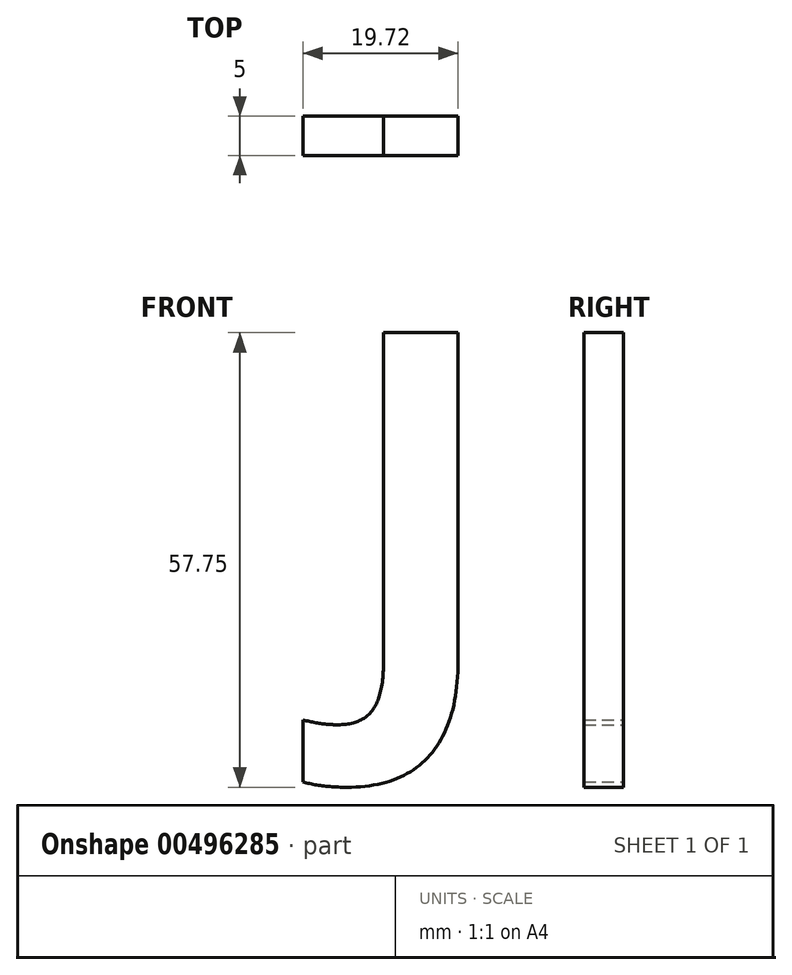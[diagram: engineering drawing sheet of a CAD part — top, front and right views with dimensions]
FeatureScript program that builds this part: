
annotation { "Feature Type Name" : "Feature", "Feature Type Description" : "" }
export const myFeature = defineFeature(function(context is Context, id is Id, definition is map)
    precondition{}
    {
        {
            var Q0;
            Q0=qCreatedBy(makeId("Front.planeOp"),FACE);
            var sketch = newSketch(context, id + "F0", { "sketchPlane" : qUnion([Q0])});
            skText(sketch, "E0", { "text": "J", "fontName": "OpenSans-Bold.ttf"});
            const initialGuessF0  = {"E0": [-0.05687, 0.00803, 1, 0, 0.045]};
            skSetInitialGuess(sketch, initialGuessF0);
            skSolve(sketch);
        }
        {
            var Q0;
            Q0=makeQuery(id+"F0.imprint","IMPRINT",FACE,{"disambiguationData":[TD([[makeQuery(id+"F0.imprint","IMPRINT",EDGE,{"derivedFrom":sQuery(id+"F0.wireOp",EDGE,"E0.sketch_text.stroke-0")}),-1.0]])]});
            extrude(context, id + "F1", {"entities" : qUnion([Q0]), "depth" : 5 * mm});
        }
    });
